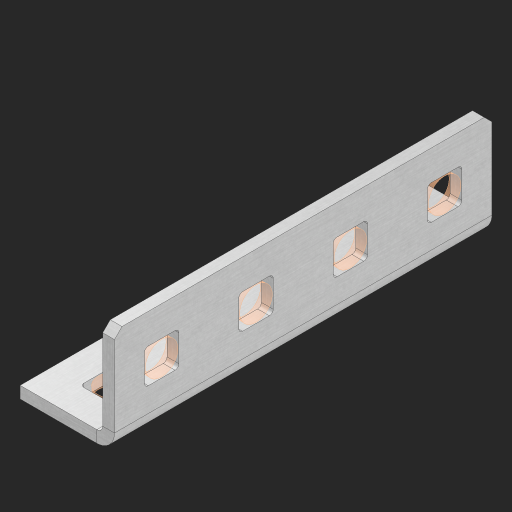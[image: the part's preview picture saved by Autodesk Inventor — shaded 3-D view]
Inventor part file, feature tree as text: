
AUTODESK INVENTOR PART (.ipt)
format: ipt  version: 2023 (Build 270158000, 158)  size: 478,208 bytes
history: native  units: in
note: dims shown in document units (in); Inventor stores cm internally (conversion verified against a paired STEP export)
features: other x13, sheet_metal_op x10, sketch x8, extrude x7, mirror x1, pattern_linear x1, chamfer x1
ambient origin geometry x8: Origin, YZ Plane, XZ Plane, XY Plane, X Axis, Y Axis, Z Axis, Center Point
bodies: Solid1 (feature_tree), Body (feature_tree)
feature tree (41):
  other  "Flange Pattern Plane"
  sheet_metal_op  "Flange Pattern"
  sheet_metal_op  "Body Pattern"
  other  "Arc Length"
  mirror  "Notch Mirror"
  pattern_linear  "Notch Pattern"  Spacing1=0.25in  [1 undecoded]
  chamfer  "End Chamfer"
  extrude  "Half Cut"  Depth=0.0625in
  sketch  "Sketch1"  dims[d0=1.5in]
  other  "Plate1"
  sketch  "Sketch2"  dims[d1=2.0in]
  other  "Plate2"
  sheet_metal_op  "Bend1"
  sheet_metal_op  "Corner1"
  sketch  "Sketch3"  dims[d2=0.0625in]
  other  "Flange Pattern Sketch"
  sketch  "Sketch7"  dims[d3=0.0625in]
  other  "Srf1"
  other  "Srf2"
  sketch  "Sketch8"  dims[d4=0.0312in]
  sketch  "Sketch9"  dims[d5=0.125in]
  other  "Srf91"
  sheet_metal_op  "Body Pattern Sketch"
  other  "Srf92"
  sketch  "Sketch13"  dims[d6=0.0625in]
  sketch  "Sketch14"  dims[d7=0.5in d8=90.0deg d9=0.0312in d10=0.25in d11=0.0625in d12=0.0625in d16=0.182in d17=0.02in d18=0.0625in d19=0.0in d20=0.25in d21=0.25in d46=0.172in d47=1.0in d48=0.0in d49=0.182in d50=0.02in d51=0.25in d52=0.25in d53=0.0625in d54=0.0in d55=0.172in d56=1.0in d57=0.0in d60=1.5748in d62=0.5in d63=0.3937in d65=0.5in d85=0.1473in d86=0.1782in d88=0.04in d89=0.0625in d90=0.0in d91=0.04in d92=0.0491in d95=2.5in d96=0.04in d97=0.25in d98=45.0deg d101=0.0in d102=2.497in d131=0.5in d132=1.5748in d134=0.5in d139=0.5in]
  other  "Srf856"
  other  "Srf1310"
  other  "Srf1311"
  other  "Srf1376"
  sheet_metal_op  "Flange Stamp"
  sheet_metal_op  "Flange Circle"
  sheet_metal_op  "Body Stamp"
  sheet_metal_op  "Body Circle"
  sheet_metal_op  "Notch"
  extrude  "ExtrusionSrf2"  Depth=0.0625in
  extrude  "ExtrusionSrf92"  Depth=0.182in
  extrude  "ExtrusionSrf856"  Depth=0.02in
  extrude  "ExtrusionSrf1310"  Depth=0.0625in
  extrude  "ExtrusionSrf1311"  TaperAngle=0.0deg  [1 undecoded]
  extrude  "ExtrusionSrf1376"  Depth=0.5in
note: 2 required parameter values undecoded (feature->parameter linkage not recoverable at this tier; creation-order binding heuristic only, values carry confidence <= 0.55)
